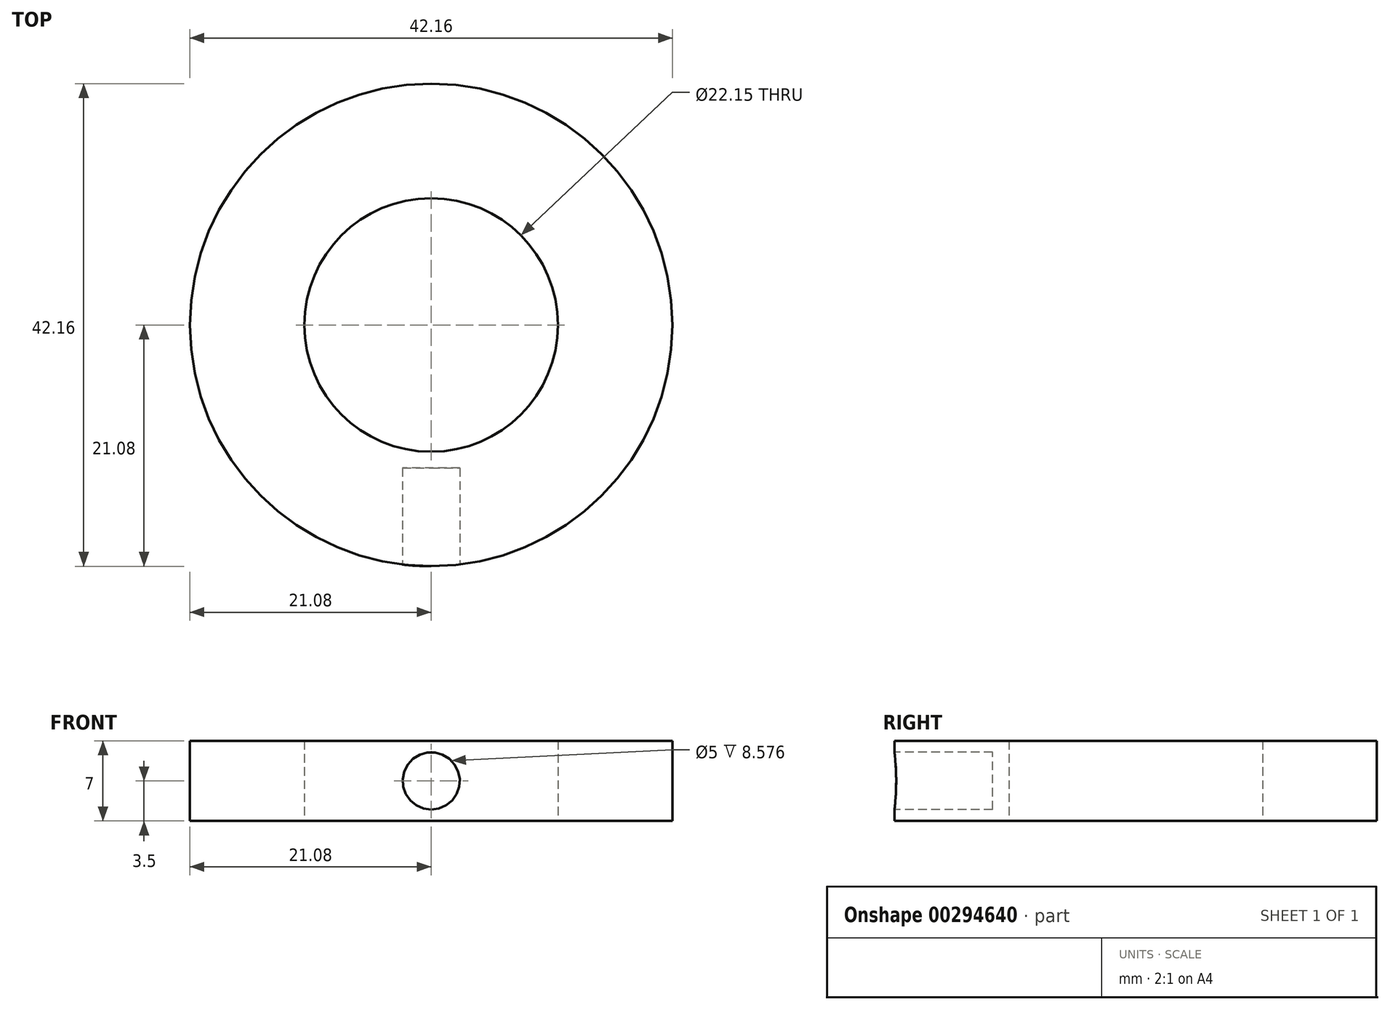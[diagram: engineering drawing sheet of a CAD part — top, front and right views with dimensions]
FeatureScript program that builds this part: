
annotation { "Feature Type Name" : "Feature", "Feature Type Description" : "" }
export const myFeature = defineFeature(function(context is Context, id is Id, definition is map)
    precondition{}
    {
        {
            var Q0;
            Q0=qCreatedBy(makeId("Top.planeOp"),FACE);
            var sketch = newSketch(context, id + "F0", { "sketchPlane" : qUnion([Q0])});
            skCircle(sketch, "E0", {"center": v(0, 0) * mm, "radius": 11.08 * mm});
            skCircle(sketch, "E1", {"center": v(0, 0) * mm, "radius": 21.07 * mm});
            skSolve(sketch);
        }
        {
            var Q0;
            Q0=makeQuery(id+"F0.imprint","IMPRINT",FACE,{"disambiguationData":[TD([[makeQuery(id+"F0.imprint","IMPRINT",EDGE,{"derivedFrom":sQuery(id+"F0.wireOp",EDGE,"E0")}),-1.0]])]});
            extrude(context, id + "F1", {"entities" : qUnion([Q0]), "depth" : 7 * mm});
        }
        {
            var Q0;
            Q0=qCreatedBy(makeId("Front.planeOp"),FACE);
            cPlane(context, id + "F2", {"entities" : qUnion([Q0]), "cplaneType" : CPlaneType.OFFSET, "offset" : 25 * mm, "width" : 150 * mm, "height" : 150 * mm});
        }
        {
            var Q0;
            Q0=qCreatedBy(id+"F2.planeOp",FACE);
            var sketch = newSketch(context, id + "F3", { "sketchPlane" : qUnion([Q0])});
            skCircle(sketch, "E2", {"center": v(0, 3.5) * mm, "radius": 2.5 * mm});
            skLineSegment(sketch, "E3", {"start": v(0, 0) * mm, "end": v(0, 7) * mm});
            skSolve(sketch);
        }
        {
            var Q0;
            {var subQ0=sQuery(id+"F3.wireOp",EDGE,"E3");var subQ1=sQuery(id+"F3.wireOp",EDGE,"E2");var subQ2=makeQuery(id+"F3.imprint","INTERSECT",VERTEX,{"disambiguationData":[OD(0.0)],"derivedFrom":[subQ1,subQ0]});Q0=makeQuery(id+"F3.imprint","IMPRINT",FACE,{"disambiguationData":[TD([[makeQuery(id+"F3.imprint","IMPRINT",EDGE,{"disambiguationData":[TD([[subQ2,-1.0]])],"derivedFrom":subQ1}),1.0]])]});}
            var Q1;
            {var subQ0=sQuery(id+"F3.wireOp",EDGE,"E3");var subQ1=sQuery(id+"F3.wireOp",EDGE,"E2");var subQ2=makeQuery(id+"F3.imprint","INTERSECT",VERTEX,{"disambiguationData":[OD(0.0)],"derivedFrom":[subQ1,subQ0]});Q1=makeQuery(id+"F3.imprint","IMPRINT",FACE,{"disambiguationData":[TD([[makeQuery(id+"F3.imprint","IMPRINT",EDGE,{"disambiguationData":[TD([[subQ2,1.0]])],"derivedFrom":subQ1}),1.0]])]});}
            extrude(context, id + "F4", {"entities" : qUnion([Q0, Q1]), "operationType" : NewBodyOperationType.REMOVE, "oppositeDirection" : true, "depth" : 12.5 * mm});
        }
    });
